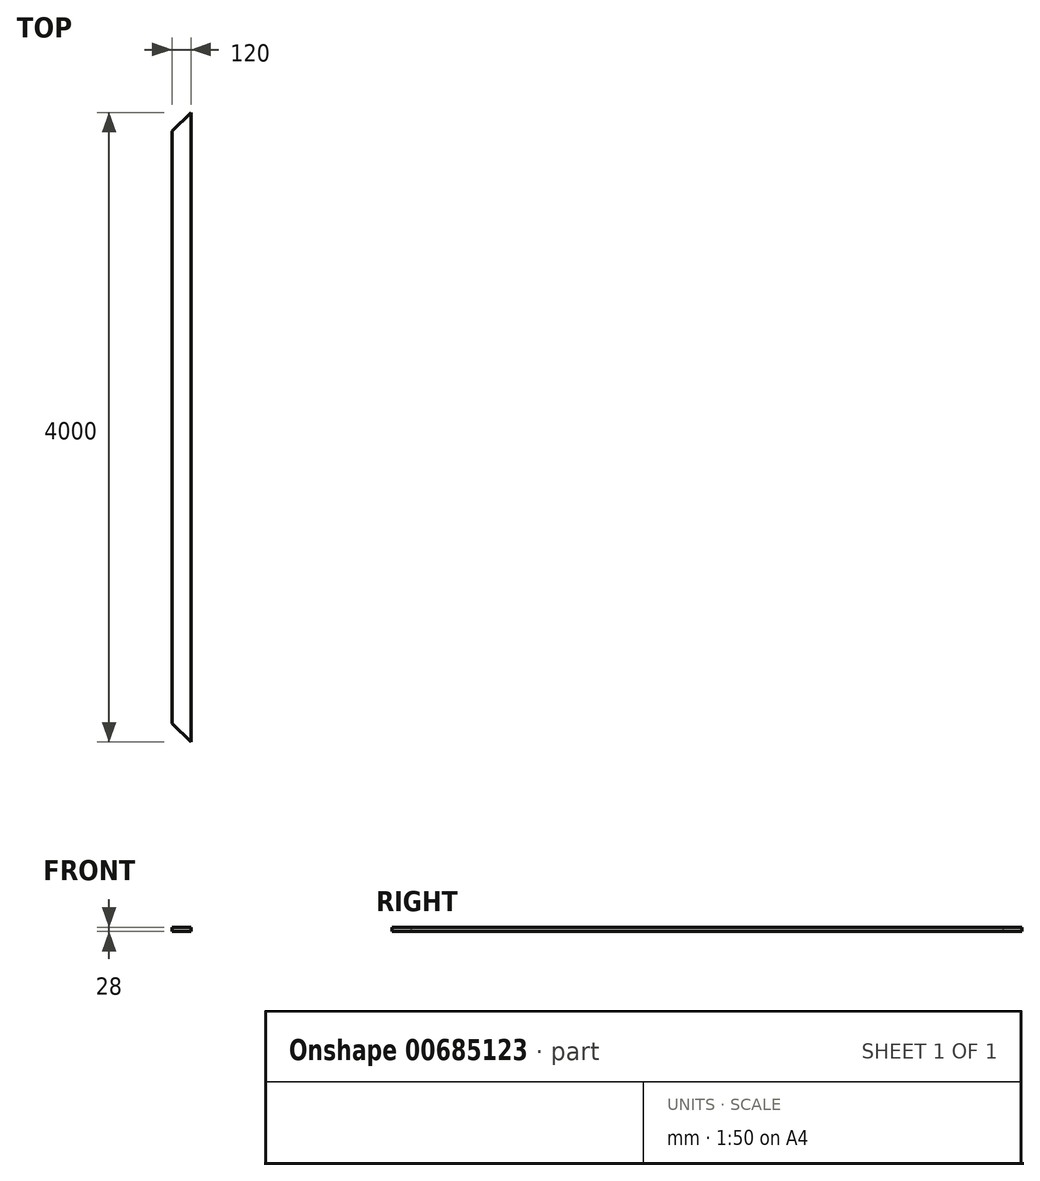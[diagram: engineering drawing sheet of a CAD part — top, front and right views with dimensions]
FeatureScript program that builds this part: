
annotation { "Feature Type Name" : "Feature", "Feature Type Description" : "" }
export const myFeature = defineFeature(function(context is Context, id is Id, definition is map)
    precondition{}
    {
        {
            var Q0;
            Q0=qCreatedBy(makeId("Top.planeOp"),FACE);
            var sketch = newSketch(context, id + "F0", { "sketchPlane" : qUnion([Q0])});
            skLineSegment(sketch, "E0", {"start": v(41.39, -935.05) * mm, "end": v(41.39, 3064.95) * mm});
            skLineSegment(sketch, "E1", {"start": v(41.39, 3064.95) * mm, "end": v(-78.61, 2944.95) * mm});
            skLineSegment(sketch, "E2", {"start": v(-78.61, 2944.95) * mm, "end": v(-78.61, -815.05) * mm});
            skLineSegment(sketch, "E3", {"start": v(-78.61, -815.05) * mm, "end": v(41.39, -935.05) * mm});
            skSolve(sketch);
        }
        {
            var Q0;
            Q0 = qSketchRegion(id + "F0", true);
            extrude(context, id + "F1", {"entities" : qUnion([Q0]), "depth" : 28 * mm, "offsetDistance" : 25 * mm});
        }
    });
